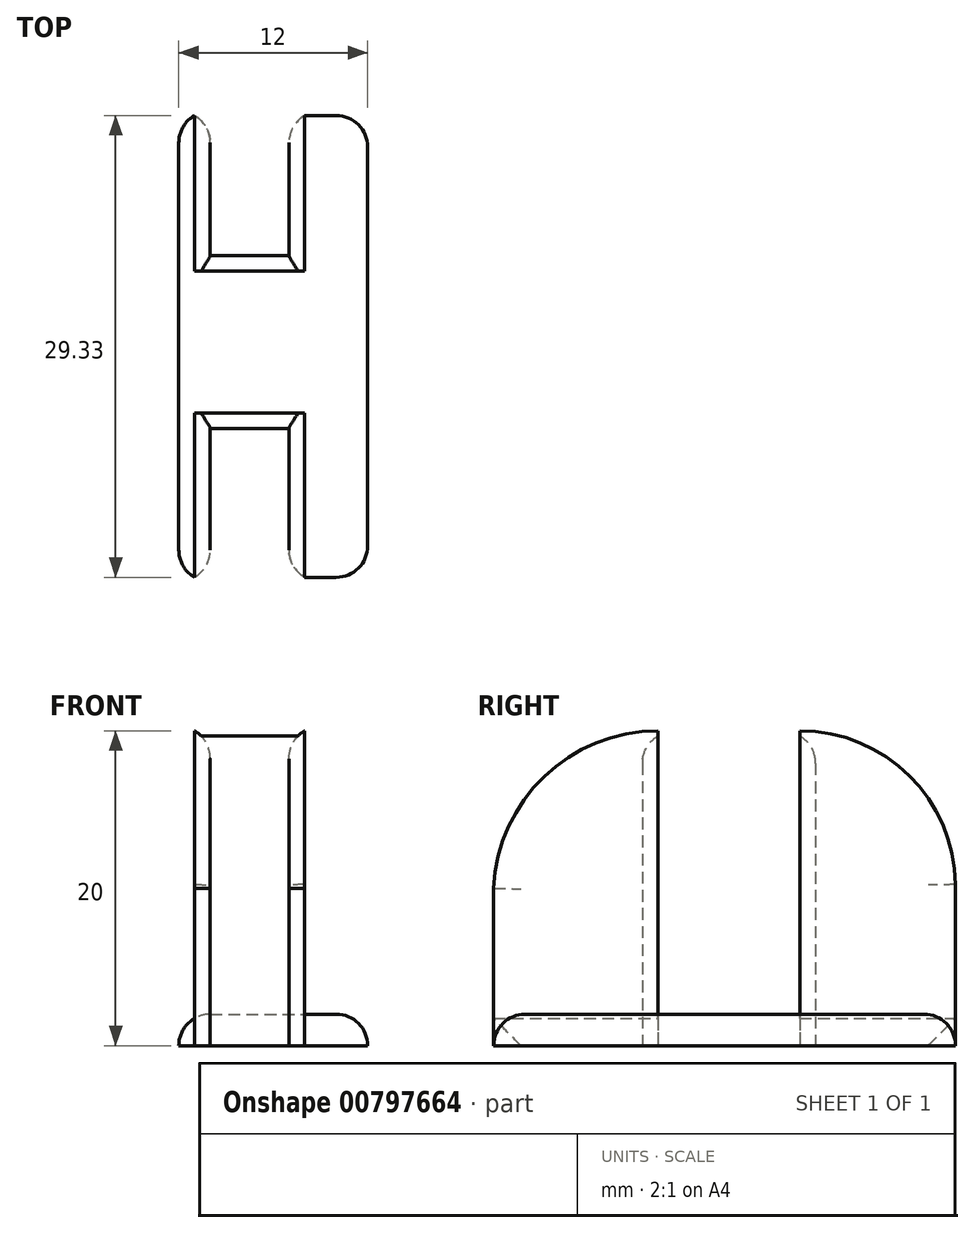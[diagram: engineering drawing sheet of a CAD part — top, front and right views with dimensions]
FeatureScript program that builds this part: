
annotation { "Feature Type Name" : "Feature", "Feature Type Description" : "" }
export const myFeature = defineFeature(function(context is Context, id is Id, definition is map)
    precondition{}
    {
        {
            var Q0;
            Q0=qCreatedBy(makeId("Top.planeOp"),FACE);
            var sketch = newSketch(context, id + "F0", { "sketchPlane" : qUnion([Q0])});
            skLineSegment(sketch, "E0.bottom", {"start": v(0, 0) * mm, "end": v(-5, 0) * mm});
            skLineSegment(sketch, "E0.top", {"start": v(0, 9.45) * mm, "end": v(-5, 9.45) * mm});
            skLineSegment(sketch, "E0.left", {"start": v(0, 0) * mm, "end": v(0, 9.45) * mm});
            skLineSegment(sketch, "E0.right", {"start": v(-5, 0) * mm, "end": v(-5, 9.45) * mm});
            skLineSegment(sketch, "E1.top", {"start": v(0, 20.45) * mm, "end": v(-5, 20.45) * mm});
            skLineSegment(sketch, "E1.left", {"start": v(0, 9.45) * mm, "end": v(0, 20.45) * mm});
            skLineSegment(sketch, "E1.right", {"start": v(-5, 9.45) * mm, "end": v(-5, 20.45) * mm});
            skLineSegment(sketch, "E2.top", {"start": v(0, 29.33) * mm, "end": v(-5, 29.33) * mm});
            skLineSegment(sketch, "E2.left", {"start": v(0, 20.45) * mm, "end": v(0, 29.33) * mm});
            skLineSegment(sketch, "E2.right", {"start": v(-5, 20.45) * mm, "end": v(-5, 29.33) * mm});
            skLineSegment(sketch, "E3.bottom", {"start": v(-5, 29.33) * mm, "end": v(-7, 29.33) * mm});
            skLineSegment(sketch, "E3.top", {"start": v(-5, 0) * mm, "end": v(-7, 0) * mm});
            skLineSegment(sketch, "E3.left", {"start": v(-5, 29.33) * mm, "end": v(-5, 0) * mm});
            skLineSegment(sketch, "E3.right", {"start": v(-7, 29.33) * mm, "end": v(-7, 0) * mm});
            skLineSegment(sketch, "E4.bottom", {"start": v(0, 0) * mm, "end": v(5, 0) * mm});
            skLineSegment(sketch, "E4.top", {"start": v(0, 29.33) * mm, "end": v(5, 29.33) * mm});
            skLineSegment(sketch, "E4.left", {"start": v(0, 0) * mm, "end": v(0, 29.33) * mm});
            skLineSegment(sketch, "E4.right", {"start": v(5, 0) * mm, "end": v(5, 29.33) * mm});
            skLineSegment(sketch, "E5", {"start": v(-5, 19.45) * mm, "end": v(0, 19.45) * mm});
            skLineSegment(sketch, "E6", {"start": v(-5, 10.45) * mm, "end": v(0, 10.45) * mm});
            skLineSegment(sketch, "E7", {"start": v(1, 29.33) * mm, "end": v(1, 0) * mm});
            skLineSegment(sketch, "E8", {"start": v(-6, 29.33) * mm, "end": v(-6, 0) * mm});
            skLineSegment(sketch, "E9", {"start": v(-5, 19.45) * mm, "end": v(-6, 19.45) * mm});
            skLineSegment(sketch, "E10", {"start": v(0, 19.45) * mm, "end": v(1, 19.45) * mm});
            skLineSegment(sketch, "E11", {"start": v(-5, 10.45) * mm, "end": v(-6, 10.45) * mm});
            skLineSegment(sketch, "E12", {"start": v(0, 10.45) * mm, "end": v(1, 10.45) * mm});
            skSolve(sketch);
        }
        {
            var Q0;
            {var subQ4=sQuery(id+"F0.wireOp",EDGE,"E0.right");Q0=makeQuery(id+"F0.imprint","IMPRINT",FACE,{"disambiguationData":[TD([[makeQuery(id+"F0.imprint","IMPRINT",EDGE,{"derivedFrom":subQ4}),1.0]])]});}
            var Q1;
            {var subQ1=sQuery(id+"F0.wireOp",EDGE,"E0.left");Q1=makeQuery(id+"F0.imprint","IMPRINT",FACE,{"disambiguationData":[TD([[makeQuery(id+"F0.imprint","IMPRINT",EDGE,{"derivedFrom":subQ1}),-1.0]])]});}
            var Q2;
            {var subQ4=sQuery(id+"F0.wireOp",EDGE,"E2.left");Q2=makeQuery(id+"F0.imprint","IMPRINT",FACE,{"disambiguationData":[TD([[makeQuery(id+"F0.imprint","IMPRINT",EDGE,{"derivedFrom":subQ4}),-1.0]])]});}
            var Q3;
            {var subQ0=sQuery(id+"F0.wireOp",EDGE,"E1.top");Q3=makeQuery(id+"F0.imprint","IMPRINT",FACE,{"disambiguationData":[TD([[makeQuery(id+"F0.imprint","IMPRINT",EDGE,{"derivedFrom":subQ0}),1.0]])]});}
            var Q4;
            {var subQ4=sQuery(id+"F0.wireOp",EDGE,"E2.right");Q4=makeQuery(id+"F0.imprint","IMPRINT",FACE,{"disambiguationData":[TD([[makeQuery(id+"F0.imprint","IMPRINT",EDGE,{"derivedFrom":subQ4}),1.0]])]});}
            var Q5;
            {var subQ0=sQuery(id+"F0.wireOp",EDGE,"E0.top");Q5=makeQuery(id+"F0.imprint","IMPRINT",FACE,{"disambiguationData":[TD([[makeQuery(id+"F0.imprint","IMPRINT",EDGE,{"derivedFrom":subQ0}),-1.0]])]});}
            extrude(context, id + "F1", {"entities" : qUnion([Q0, Q1, Q2, Q3, Q4, Q5]), "depth" : 20 * mm, "offsetDistance" : 25 * mm});
        }
        {
            var Q0;
            {var subQ0=sQuery(id+"F0.wireOp",EDGE,"E8");Q0=makeQuery(id+"F1.opExtrude","SWEPT_FACE",FACE,{"disambiguationData":[OSD([subQ0]),TDD([makeQuery(id+"F0.imprint","IMPRINT",EDGE,{"disambiguationData":[TD([[makeQuery(id+"F0.imprint","INTERSECT",VERTEX,{"derivedFrom":[sQuery(id+"F0.wireOp",EDGE,"E3.bottom"),subQ0]}),-1.0]])],"derivedFrom":subQ0})])]});}
            var sketch = newSketch(context, id + "F2", { "sketchPlane" : qUnion([Q0])});
            skArc(sketch, "E13", {"start": v(-19.45, 20) * mm, "mid": v(-26.48, 17.06) * mm, "end": v(-29.33, 10) * mm});
            skSolve(sketch);
        }
        {
            var Q0;
            Q0 = qSketchRegion(id + "F2", true);
            var Q1;
            {var subQ1=sQuery(id+"F0.wireOp",EDGE,"E8");var subQ2=sQuery(id+"F0.wireOp",EDGE,"E3.bottom");var subQ4=makeQuery(id+"F1.opExtrude","CAP_EDGE",EDGE,{"disambiguationData":[OSD([subQ1]),TDD([makeQuery(id+"F0.imprint","IMPRINT",EDGE,{"disambiguationData":[TD([[makeQuery(id+"F0.imprint","INTERSECT",VERTEX,{"derivedFrom":[subQ2,subQ1]}),-1.0]])],"derivedFrom":subQ1})])],"isStart":false});Q1=makeQuery(id+"F2.imprint","IMPRINT",FACE,{"disambiguationData":[TD([[makeQuery(id+"F2.imprint","IMPRINT",EDGE,{"derivedFrom":subQ4}),-1.0]])]});}
            extrude(context, id + "F3", {"entities" : qUnion([Q0, Q1]), "operationType" : NewBodyOperationType.REMOVE, "oppositeDirection" : true, "depth" : 25 * mm, "offsetDistance" : 25 * mm});
        }
        {
            var Q0;
            {var subQ0=sQuery(id+"F0.wireOp",EDGE,"E8");Q0=makeQuery(id+"F1.opExtrude","SWEPT_FACE",FACE,{"disambiguationData":[OSD([subQ0]),TDD([makeQuery(id+"F0.imprint","IMPRINT",EDGE,{"disambiguationData":[TD([[makeQuery(id+"F0.imprint","INTERSECT",VERTEX,{"derivedFrom":[subQ0,sQuery(id+"F0.wireOp",EDGE,"E11")]}),-1.0]])],"derivedFrom":subQ0})])]});}
            var sketch = newSketch(context, id + "F4", { "sketchPlane" : qUnion([Q0])});
            skArc(sketch, "E14", {"start": v(0, 10) * mm, "mid": v(-3.22, 17.1) * mm, "end": v(-10.45, 20) * mm});
            skSolve(sketch);
        }
        {
            var Q0;
            Q0 = qSketchRegion(id + "F4", true);
            var Q1;
            {var subQ0=sQuery(id+"F4.wireOp",EDGE,"E14");Q1=makeQuery(id+"F4.imprint","IMPRINT",FACE,{"disambiguationData":[TD([[makeQuery(id+"F4.imprint","IMPRINT",EDGE,{"derivedFrom":subQ0}),-1.0]])]});}
            extrude(context, id + "F5", {"entities" : qUnion([Q0, Q1]), "operationType" : NewBodyOperationType.REMOVE, "oppositeDirection" : true, "depth" : 25 * mm, "offsetDistance" : 25 * mm});
        }
        {
            var Q0;
            {var subQ2=sQuery(id+"F0.wireOp",EDGE,"E5");Q0=makeQuery(id+"F0.imprint","IMPRINT",FACE,{"disambiguationData":[TD([[makeQuery(id+"F0.imprint","IMPRINT",EDGE,{"derivedFrom":subQ2}),-1.0]])]});}
            var Q1;
            {var subQ2=sQuery(id+"F0.wireOp",EDGE,"E10");Q1=makeQuery(id+"F0.imprint","IMPRINT",FACE,{"disambiguationData":[TD([[makeQuery(id+"F0.imprint","IMPRINT",EDGE,{"derivedFrom":subQ2}),-1.0]])]});}
            var Q2;
            {var subQ0=sQuery(id+"F0.wireOp",EDGE,"E4.right");Q2=makeQuery(id+"F0.imprint","IMPRINT",FACE,{"disambiguationData":[TD([[makeQuery(id+"F0.imprint","IMPRINT",EDGE,{"derivedFrom":subQ0}),1.0]])]});}
            var Q3;
            {var subQ2=sQuery(id+"F0.wireOp",EDGE,"E9");Q3=makeQuery(id+"F0.imprint","IMPRINT",FACE,{"disambiguationData":[TD([[makeQuery(id+"F0.imprint","IMPRINT",EDGE,{"derivedFrom":subQ2}),1.0]])]});}
            var Q4;
            {var subQ0=sQuery(id+"F0.wireOp",EDGE,"E3.right");Q4=makeQuery(id+"F0.imprint","IMPRINT",FACE,{"disambiguationData":[TD([[makeQuery(id+"F0.imprint","IMPRINT",EDGE,{"derivedFrom":subQ0}),1.0]])]});}
            extrude(context, id + "F6", {"entities" : qUnion([Q0, Q1, Q2, Q3, Q4]), "depth" : 2 * mm, "offsetDistance" : 25 * mm});
        }
        {
            var Q0;
            Q0=makeQuery(id+"F6.opExtrude","CAP_EDGE",EDGE,{"disambiguationData":[OSD([sQuery(id+"F0.wireOp",EDGE,"E3.right")])],"isStart":false});
            var Q1;
            Q1=makeQuery(id+"F6.opExtrude","CAP_EDGE",EDGE,{"disambiguationData":[OSD([sQuery(id+"F0.wireOp",EDGE,"E4.right")])],"isStart":false});
            var Q2;
            Q2=makeQuery(id+"F1.opExtrude","SWEPT_EDGE",EDGE,{"disambiguationData":[OSD([sQuery(id+"F0.wireOp",EDGE,"E0.bottom"),sQuery(id+"F0.wireOp",EDGE,"E0.left"),sQuery(id+"F0.wireOp",EDGE,"E4.bottom")])]});
            var Q3;
            Q3=makeQuery(id+"F5.boolean.opBoolean","INTERSECT",EDGE,{"derivedFrom":[makeQuery(id+"F1.opExtrude","SWEPT_FACE",FACE,{"disambiguationData":[OSD([sQuery(id+"F0.wireOp",EDGE,"E0.left")])]}),makeQuery(id+"F5.opExtrude","SWEPT_FACE",FACE,{"disambiguationData":[OSD([sQuery(id+"F4.wireOp",EDGE,"E14")])]})]});
            var Q4;
            Q4=makeQuery(id+"F1.opExtrude","SWEPT_EDGE",EDGE,{"disambiguationData":[OSD([sQuery(id+"F0.wireOp",EDGE,"E0.bottom"),sQuery(id+"F0.wireOp",EDGE,"E0.right"),sQuery(id+"F0.wireOp",EDGE,"E3.top")])]});
            var Q5;
            Q5=makeQuery(id+"F5.boolean.opBoolean","INTERSECT",EDGE,{"derivedFrom":[makeQuery(id+"F1.opExtrude","SWEPT_FACE",FACE,{"disambiguationData":[OSD([sQuery(id+"F0.wireOp",EDGE,"E0.right")])]}),makeQuery(id+"F5.opExtrude","SWEPT_FACE",FACE,{"disambiguationData":[OSD([sQuery(id+"F4.wireOp",EDGE,"E14")])]})]});
            var Q6;
            Q6=makeQuery(id+"F3.boolean.opBoolean","INTERSECT",EDGE,{"derivedFrom":[makeQuery(id+"F1.opExtrude","SWEPT_FACE",FACE,{"disambiguationData":[OSD([sQuery(id+"F0.wireOp",EDGE,"E1.top")])]}),makeQuery(id+"F3.opExtrude","SWEPT_FACE",FACE,{"disambiguationData":[OSD([sQuery(id+"F2.wireOp",EDGE,"E13")])]})]});
            var Q7;
            Q7=makeQuery(id+"F5.boolean.opBoolean","INTERSECT",EDGE,{"derivedFrom":[makeQuery(id+"F1.opExtrude","SWEPT_FACE",FACE,{"disambiguationData":[OSD([sQuery(id+"F0.wireOp",EDGE,"E0.top")])]}),makeQuery(id+"F5.opExtrude","SWEPT_FACE",FACE,{"disambiguationData":[OSD([sQuery(id+"F4.wireOp",EDGE,"E14")])]})]});
            var Q8;
            Q8=makeQuery(id+"F3.boolean.opBoolean","INTERSECT",EDGE,{"derivedFrom":[makeQuery(id+"F1.opExtrude","SWEPT_FACE",FACE,{"disambiguationData":[OSD([sQuery(id+"F0.wireOp",EDGE,"E2.left")])]}),makeQuery(id+"F3.opExtrude","SWEPT_FACE",FACE,{"disambiguationData":[OSD([sQuery(id+"F2.wireOp",EDGE,"E13")])]})]});
            var Q9;
            Q9=makeQuery(id+"F1.opExtrude","SWEPT_EDGE",EDGE,{"disambiguationData":[OSD([sQuery(id+"F0.wireOp",EDGE,"E2.top"),sQuery(id+"F0.wireOp",EDGE,"E2.left"),sQuery(id+"F0.wireOp",EDGE,"E4.top")])]});
            var Q10;
            Q10=makeQuery(id+"F1.opExtrude","SWEPT_EDGE",EDGE,{"disambiguationData":[OSD([sQuery(id+"F0.wireOp",EDGE,"E2.top"),sQuery(id+"F0.wireOp",EDGE,"E2.right"),sQuery(id+"F0.wireOp",EDGE,"E3.bottom")])]});
            var Q11;
            Q11=makeQuery(id+"F3.boolean.opBoolean","INTERSECT",EDGE,{"derivedFrom":[makeQuery(id+"F1.opExtrude","SWEPT_FACE",FACE,{"disambiguationData":[OSD([sQuery(id+"F0.wireOp",EDGE,"E2.right")])]}),makeQuery(id+"F3.opExtrude","SWEPT_FACE",FACE,{"disambiguationData":[OSD([sQuery(id+"F2.wireOp",EDGE,"E13")])]})]});
            var Q12;
            Q12=makeQuery(id+"F6.opExtrude","CAP_EDGE",EDGE,{"disambiguationData":[OSD([sQuery(id+"F0.wireOp",EDGE,"E4.top")])],"isStart":false});
            var Q13;
            Q13=makeQuery(id+"F6.opExtrude","SWEPT_EDGE",EDGE,{"disambiguationData":[OSD([sQuery(id+"F0.wireOp",EDGE,"E3.bottom"),sQuery(id+"F0.wireOp",EDGE,"E3.right")])]});
            var Q14;
            Q14=makeQuery(id+"F6.opExtrude","SWEPT_EDGE",EDGE,{"disambiguationData":[OSD([sQuery(id+"F0.wireOp",EDGE,"E3.top"),sQuery(id+"F0.wireOp",EDGE,"E3.right")])]});
            var Q15;
            Q15=makeQuery(id+"F6.opExtrude","SWEPT_EDGE",EDGE,{"disambiguationData":[OSD([sQuery(id+"F0.wireOp",EDGE,"E4.bottom"),sQuery(id+"F0.wireOp",EDGE,"E4.right")])]});
            var Q16;
            Q16=makeQuery(id+"F6.opExtrude","CAP_EDGE",EDGE,{"disambiguationData":[OSD([sQuery(id+"F0.wireOp",EDGE,"E4.bottom")])],"isStart":false});
            var Q17;
            Q17=makeQuery(id+"F6.opExtrude","SWEPT_EDGE",EDGE,{"disambiguationData":[OSD([sQuery(id+"F0.wireOp",EDGE,"E4.top"),sQuery(id+"F0.wireOp",EDGE,"E4.right")])]});
            fillet(context, id + "F7", {"entities" : qUnion([Q0, Q1, Q2, Q3, Q4, Q5, Q6, Q7, Q8, Q9, Q10, Q11, Q12, Q13, Q14, Q15, Q16, Q17]), "radius" : 2 * mm, "tangentPropagation" : true, "allowEdgeOverflow" : false});
        }
    });
